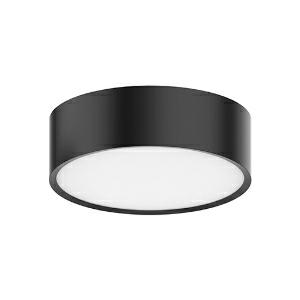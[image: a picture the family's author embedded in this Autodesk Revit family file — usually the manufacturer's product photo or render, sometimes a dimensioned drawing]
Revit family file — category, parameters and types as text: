
# Revit family: ledceilinglu-e_rd142-24w-840-bl_540001296200
name_source: partatom
category: Leuchten
revit_build: Autodesk Revit 2016 (Build: 20190508_0715(x64)
units: mm (PartAtom-declared; Revit-internal decimal feet)

## family parameters
Basisbauteil = Fläche
Beim Laden mit Abzugskörper schneiden = Nein
Bemaßung runder Anschluss = Durchmesser verwenden
Gemeinsam genutzt = Nein
Lichtquelle = Nein
Raumberechnungspunkt = Nein
Teiletyp = Normal

## types (1)
- LEDCeilingLu-E Rd142-24W-840-BL (1 x LED, 2160 lm)
    Approval mark = CE
    Beschreibung = Stylish and compact ceiling luminaire. Clean “twist-and-lock” mounting system. High quality full metal body. Low height of only 46mm. Suitable for ceiling and wall mounting.
    CIE Flux Codes = 49 79 96 100 100
    Control Gear = Electronic ballast
    Height = 100 mm  [stored 0.328084 ft]
    Hersteller = OPPLE
    Lamp Light Flux = 2160 lm
    Lamp count = 1
    Lampe = 1 x LED
    Length = 100 mm  [stored 0.328084 ft]
    Luminous efficacy = 90 lm/W
    ModVariant = Nein
    Modell = 540001296200
    Mounting Place = Wall, Ceiling
    Mounting Type = Surface mounted
    Number of Poles = 1
    OnlyDefault = Ja
    Power Factor = 1
    Product Name = LEDCeilingLu-E Rd142-24W-840-BL
    Product group = Ceiling Light Luna
    ProductGroupID = 305
    Protection Class = Protection class II
    Protection Degree = IP 20
    RLX_Detail_Level = 1
    RlxData = <blob elided: 129533 chars, md5=6e082d51>
    Scheinlast = 24 VA
    Socket = socket
    Standby Power = 0 W
    System Light Flux = 2160 lm
    System Power = 24 W
    Typenbild = luna_bl_rd142.jpg
    Typenkommentare = Product without accessories
    URL = http://relux.com
    VarID = ---
    Voltage = 230 V
    Voltage Range = 220-240 V
    Vorgabe-Ansicht = 1800 mm
    Weight = 0.00 kg
    Width = 100 mm  [stored 0.328084 ft]

note: [stored X ft] marks values corroborated as IEEE doubles in the binary element streams (Revit-internal decimal feet)

## geometry (parser evidence)
native form markers: Blend x4, Sweep x12
no freeform markers — native parametric forms only
